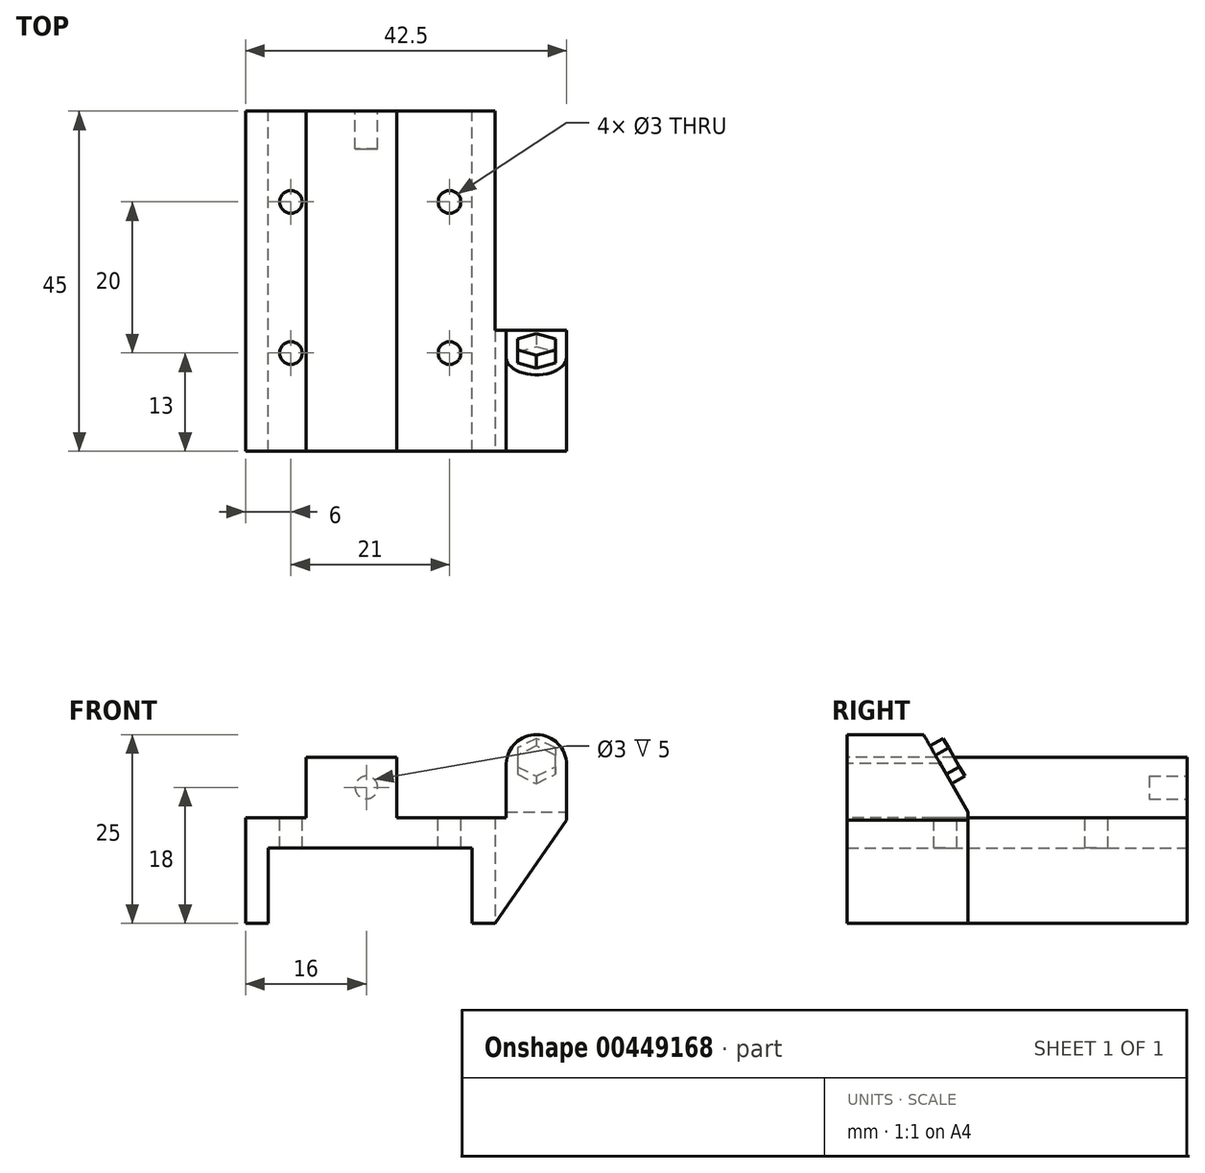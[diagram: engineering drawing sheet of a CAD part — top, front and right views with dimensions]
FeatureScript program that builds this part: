
annotation { "Feature Type Name" : "Feature", "Feature Type Description" : "" }
export const myFeature = defineFeature(function(context is Context, id is Id, definition is map)
    precondition{}
    {
        {
            var Q0;
            Q0=qCreatedBy(makeId("Top.planeOp"),FACE);
            var sketch = newSketch(context, id + "F0", { "sketchPlane" : qUnion([Q0]), "disableImprinting" : false});
            skLineSegment(sketch, "E0.bottom", {"start": v(-16.5, 22.5) * mm, "end": v(16.5, 22.5) * mm});
            skLineSegment(sketch, "E0.top", {"start": v(-16.5, -22.5) * mm, "end": v(16.5, -22.5) * mm});
            skLineSegment(sketch, "E0.left", {"start": v(-16.5, 22.5) * mm, "end": v(-16.5, -22.5) * mm});
            skLineSegment(sketch, "E0.right", {"start": v(16.5, 22.5) * mm, "end": v(16.5, -22.5) * mm});
            skPoint(sketch, "E1", {"position": v(0, 22.5) * mm});
            skPoint(sketch, "E2", {"position": v(16.5, 0) * mm});
            skSolve(sketch);
        }
        {
            var Q0;
            Q0=makeQuery(id+"F0.imprint","IMPRINT",FACE,{"disambiguationData":[TD([[makeQuery(id+"F0.imprint","IMPRINT",EDGE,{"derivedFrom":sQuery(id+"F0.wireOp",EDGE,"E0.bottom")}),-1.0]])]});
            extrude(context, id + "F1", {"entities" : qUnion([Q0]), "depth" : 14 * mm});
        }
        {
            var Q0;
            Q0=makeQuery(id+"F1.opExtrude","CAP_FACE",FACE,{"disambiguationData":[OSD([sQuery(id+"F0.wireOp",EDGE,"E0.bottom"),sQuery(id+"F0.wireOp",EDGE,"E0.top"),sQuery(id+"F0.wireOp",EDGE,"E0.left"),sQuery(id+"F0.wireOp",EDGE,"E0.right")])],"isStart":true});
            var sketch = newSketch(context, id + "F2", { "sketchPlane" : qUnion([Q0]), "disableImprinting" : false});
            skLineSegment(sketch, "E3.bottom", {"start": v(-13.5, 33.53) * mm, "end": v(13.5, 33.53) * mm});
            skLineSegment(sketch, "E3.top", {"start": v(-13.5, -30.84) * mm, "end": v(13.5, -30.84) * mm});
            skLineSegment(sketch, "E3.left", {"start": v(-13.5, 33.53) * mm, "end": v(-13.5, -30.84) * mm});
            skLineSegment(sketch, "E3.right", {"start": v(13.5, 33.53) * mm, "end": v(13.5, -30.84) * mm});
            skPoint(sketch, "E4", {"position": v(0, 33.53) * mm});
            skSolve(sketch);
        }
        {
            var Q0;
            {var subQ0=sQuery(id+"F2.wireOp",EDGE,"E3.bottom");Q0=makeQuery(id+"F2.imprint","IMPRINT",FACE,{"disambiguationData":[TD([[makeQuery(id+"F2.imprint","IMPRINT",EDGE,{"derivedFrom":subQ0}),-1.0]])]});}
            var Q1;
            {var subQ0=sQuery(id+"F2.wireOp",EDGE,"E3.left");var subQ1=makeQuery(id+"F1.opExtrude","CAP_EDGE",EDGE,{"disambiguationData":[OSD([sQuery(id+"F0.wireOp",EDGE,"E0.top")])],"isStart":true});var subQ2=makeQuery(id+"F2.imprint","INTERSECT",VERTEX,{"derivedFrom":[subQ1,subQ0]});Q1=makeQuery(id+"F2.imprint","IMPRINT",FACE,{"disambiguationData":[TD([[makeQuery(id+"F2.imprint","IMPRINT",EDGE,{"disambiguationData":[TD([[subQ2,-1.0]])],"derivedFrom":subQ0}),1.0]])]});}
            var Q2;
            {var subQ0=sQuery(id+"F2.wireOp",EDGE,"E3.top");Q2=makeQuery(id+"F2.imprint","IMPRINT",FACE,{"disambiguationData":[TD([[makeQuery(id+"F2.imprint","IMPRINT",EDGE,{"derivedFrom":subQ0}),1.0]])]});}
            extrude(context, id + "F3", {"entities" : qUnion([Q0, Q1, Q2]), "operationType" : NewBodyOperationType.REMOVE, "oppositeDirection" : true, "depth" : 10 * mm});
        }
        {
            var Q0;
            Q0=makeQuery(id+"F1.opExtrude","CAP_FACE",FACE,{"disambiguationData":[OSD([sQuery(id+"F0.wireOp",EDGE,"E0.bottom"),sQuery(id+"F0.wireOp",EDGE,"E0.top"),sQuery(id+"F0.wireOp",EDGE,"E0.left"),sQuery(id+"F0.wireOp",EDGE,"E0.right")])],"isStart":false});
            var sketch = newSketch(context, id + "F4", { "sketchPlane" : qUnion([Q0])});
            skLineSegment(sketch, "E5.bottom", {"start": v(3.5, 22.5) * mm, "end": v(-8.5, 22.5) * mm});
            skLineSegment(sketch, "E5.top", {"start": v(3.5, -22.5) * mm, "end": v(-8.5, -22.5) * mm});
            skLineSegment(sketch, "E5.left", {"start": v(3.5, 22.5) * mm, "end": v(3.5, -22.5) * mm});
            skLineSegment(sketch, "E5.right", {"start": v(-8.5, 22.5) * mm, "end": v(-8.5, -22.5) * mm});
            skSolve(sketch);
        }
        {
            var Q0;
            Q0=makeQuery(id+"F4.imprint","IMPRINT",FACE,{"disambiguationData":[TD([[makeQuery(id+"F4.imprint","IMPRINT",EDGE,{"derivedFrom":sQuery(id+"F4.wireOp",EDGE,"E5.bottom")}),-1.0]])]});
            extrude(context, id + "F5", {"entities" : qUnion([Q0]), "operationType" : NewBodyOperationType.ADD, "depth" : 8 * mm});
        }
        {
            var Q0;
            {var subQ0=sQuery(id+"F0.wireOp",EDGE,"E0.right");var subQ1=sQuery(id+"F0.wireOp",EDGE,"E0.top");var subQ2=sQuery(id+"F0.wireOp",EDGE,"E0.bottom");Q0=makeQuery(id+"F5.boolean.opBoolean","SPLIT",FACE,{"disambiguationData":[TD([makeQuery(id+"F1.opExtrude","SWEPT_FACE",FACE,{"disambiguationData":[OSD([subQ0])]})])],"derivedFrom":makeQuery(id+"F1.opExtrude","CAP_FACE",FACE,{"disambiguationData":[OSD([subQ2,subQ1,sQuery(id+"F0.wireOp",EDGE,"E0.left"),subQ0])],"isStart":false})});}
            var sketch = newSketch(context, id + "F6", { "sketchPlane" : qUnion([Q0])});
            skCircle(sketch, "E6", {"center": v(10.5, -9.5) * mm, "radius": 1.5 * mm});
            skCircle(sketch, "E7", {"center": v(10.5, 10.5) * mm, "radius": 1.5 * mm});
            skCircle(sketch, "E8", {"center": v(-10.5, 10.5) * mm, "radius": 1.5 * mm});
            skCircle(sketch, "E9", {"center": v(-10.5, -9.5) * mm, "radius": 1.5 * mm});
            skSolve(sketch);
        }
        {
            var Q0;
            Q0=makeQuery(id+"F6.imprint","IMPRINT",FACE,{"disambiguationData":[TD([[makeQuery(id+"F6.imprint","IMPRINT",EDGE,{"derivedFrom":sQuery(id+"F6.wireOp",EDGE,"E7")}),1.0]])]});
            var Q1;
            Q1=makeQuery(id+"F6.imprint","IMPRINT",FACE,{"disambiguationData":[TD([[makeQuery(id+"F6.imprint","IMPRINT",EDGE,{"derivedFrom":sQuery(id+"F6.wireOp",EDGE,"E6")}),1.0]])]});
            var Q2;
            Q2=makeQuery(id+"F6.imprint","IMPRINT",FACE,{"disambiguationData":[TD([[makeQuery(id+"F6.imprint","IMPRINT",EDGE,{"derivedFrom":sQuery(id+"F6.wireOp",EDGE,"E9")}),1.0]])]});
            var Q3;
            Q3=makeQuery(id+"F6.imprint","IMPRINT",FACE,{"disambiguationData":[TD([[makeQuery(id+"F6.imprint","IMPRINT",EDGE,{"derivedFrom":sQuery(id+"F6.wireOp",EDGE,"E8")}),1.0]])]});
            extrude(context, id + "F7", {"entities" : qUnion([Q0, Q1, Q2, Q3]), "operationType" : NewBodyOperationType.REMOVE, "oppositeDirection" : true, "depth" : 25 * mm});
        }
        {
            var Q0;
            Q0=makeQuery(id+"F5.boolean.opBoolean","MERGE",FACE,{"derivedFrom":[makeQuery(id+"F1.opExtrude","SWEPT_FACE",FACE,{"disambiguationData":[OSD([sQuery(id+"F0.wireOp",EDGE,"E0.bottom")])]}),makeQuery(id+"F5.opExtrude","SWEPT_FACE",FACE,{"disambiguationData":[OSD([sQuery(id+"F4.wireOp",EDGE,"E5.bottom")])]})]});
            var sketch = newSketch(context, id + "F8", { "sketchPlane" : qUnion([Q0])});
            skCircle(sketch, "E10", {"center": v(0.5, 18) * mm, "radius": 1.5 * mm});
            skSolve(sketch);
        }
        {
            var Q0;
            Q0=makeQuery(id+"F8.imprint","IMPRINT",FACE,{"disambiguationData":[TD([[makeQuery(id+"F8.imprint","IMPRINT",EDGE,{"derivedFrom":sQuery(id+"F8.wireOp",EDGE,"E10")}),1.0]])]});
            extrude(context, id + "F9", {"entities" : qUnion([Q0]), "operationType" : NewBodyOperationType.REMOVE, "oppositeDirection" : true, "depth" : 5 * mm});
        }
        {
            var Q0;
            Q0=makeQuery(id+"F5.boolean.opBoolean","MERGE",FACE,{"derivedFrom":[makeQuery(id+"F1.opExtrude","SWEPT_FACE",FACE,{"disambiguationData":[OSD([sQuery(id+"F0.wireOp",EDGE,"E0.top")])]}),makeQuery(id+"F5.opExtrude","SWEPT_FACE",FACE,{"disambiguationData":[OSD([sQuery(id+"F4.wireOp",EDGE,"E5.top")])]})]});
            var sketch = newSketch(context, id + "F10", { "sketchPlane" : qUnion([Q0])});
            skSolve(sketch);
        }
        {
            var Q0;
            {var subQ0=sQuery(id+"F4.wireOp",EDGE,"E5.top");Q0=makeQuery(id+"F10.imprint","IMPRINT",FACE,{"disambiguationData":[TD([[makeQuery(id+"F10.imprint","IMPRINT",EDGE,{"derivedFrom":makeQuery(id+"F5.opExtrude","CAP_EDGE",EDGE,{"disambiguationData":[OSD([subQ0])],"isStart":false})}),-1.0]])]});}
            var sketch = newSketch(context, id + "F11", { "sketchPlane" : qUnion([Q0])});
            skLineSegment(sketch, "E11.0", {"start": v(3.5, 14) * mm, "end": v(16.5, 14) * mm});
            skPoint(sketch, "E12.0", {"position": v(-12.5, 14) * mm});
            skLineSegment(sketch, "E13.0", {"start": v(-16.5, 14) * mm, "end": v(-8.5, 14) * mm});
            skLineSegment(sketch, "E14", {"start": v(26, 14) * mm, "end": v(26, 13.68) * mm});
            skLineSegment(sketch, "E15.0", {"start": v(13.5, 0) * mm, "end": v(13.5, 10) * mm});
            skPoint(sketch, "E16.0", {"position": v(16.5, 0) * mm});
            skLineSegment(sketch, "E17", {"start": v(16.5, 0) * mm, "end": v(26, 13.68) * mm});
            skLineSegment(sketch, "E18", {"start": v(16.5, 14) * mm, "end": v(26, 14) * mm});
            skPoint(sketch, "E19.orphan", {"position": v(26, 14.32) * mm});
            skSolve(sketch);
        }
        {
            var Q0;
            Q0=makeQuery(id+"F11.imprint","IMPRINT",FACE,{"disambiguationData":[TD([[makeQuery(id+"F11.imprint","IMPRINT",EDGE,{"derivedFrom":sQuery(id+"F11.wireOp",EDGE,"E14")}),-1.0]])]});
            extrude(context, id + "F12", {"entities" : qUnion([Q0]), "operationType" : NewBodyOperationType.ADD, "oppositeDirection" : true, "depth" : 16 * mm});
        }
        {
            var Q0;
            {var subQ0=sQuery(id+"F0.wireOp",EDGE,"E0.top");Q0=makeQuery(id+"F12.boolean.opBoolean","MERGE",FACE,{"derivedFrom":[makeQuery(id+"F5.boolean.opBoolean","MERGE",FACE,{"derivedFrom":[makeQuery(id+"F1.opExtrude","SWEPT_FACE",FACE,{"disambiguationData":[OSD([subQ0])]}),makeQuery(id+"F5.opExtrude","SWEPT_FACE",FACE,{"disambiguationData":[OSD([sQuery(id+"F4.wireOp",EDGE,"E5.top")])]})]}),makeQuery(id+"F12.opExtrude","CAP_FACE",FACE,{"disambiguationData":[OSD([subQ0,sQuery(id+"F0.wireOp",EDGE,"E0.right"),sQuery(id+"F11.wireOp",EDGE,"E14"),sQuery(id+"F11.wireOp",EDGE,"E17"),sQuery(id+"F11.wireOp",EDGE,"E18")])],"isStart":true})]});}
            var sketch = newSketch(context, id + "F13", { "sketchPlane" : qUnion([Q0])});
            skArc(sketch, "E20", {"start": v(26, 21) * mm, "mid": v(21.93, 25) * mm, "end": v(18, 20.85) * mm});
            skLineSegment(sketch, "E21", {"start": v(26, 14) * mm, "end": v(26, 21) * mm});
            skLineSegment(sketch, "E22", {"start": v(18, 21.15) * mm, "end": v(18, 14) * mm});
            skLineSegment(sketch, "E23", {"start": v(18, 14) * mm, "end": v(26, 14) * mm});
            skSolve(sketch);
        }
        {
            var Q0;
            {var subQ7=sQuery(id+"F13.wireOp",EDGE,"E21");Q0=makeQuery(id+"F13.imprint","IMPRINT",FACE,{"disambiguationData":[TD([[makeQuery(id+"F13.imprint","IMPRINT",EDGE,{"derivedFrom":subQ7}),1.0]])]});}
            extrude(context, id + "F14", {"entities" : qUnion([Q0]), "operationType" : NewBodyOperationType.ADD, "oppositeDirection" : true, "depth" : 16 * mm});
        }
        {
            var Q0;
            Q0=makeQuery(id+"F14.boolean.opBoolean","MERGE",FACE,{"derivedFrom":[makeQuery(id+"F12.opExtrude","SWEPT_FACE",FACE,{"disambiguationData":[OSD([sQuery(id+"F11.wireOp",EDGE,"E14")])]}),makeQuery(id+"F14.opExtrude","SWEPT_FACE",FACE,{"disambiguationData":[OSD([sQuery(id+"F13.wireOp",EDGE,"E21")])]})]});
            var sketch = newSketch(context, id + "F15", { "sketchPlane" : qUnion([Q0])});
            skLineSegment(sketch, "E24", {"start": v(-15.02, 29.54) * mm, "end": v(-4.6, 11.5) * mm});
            skLineSegment(sketch, "E25", {"start": v(-4.6, 11.5) * mm, "end": v(5.55, 17.37) * mm});
            skLineSegment(sketch, "E26", {"start": v(5.55, 17.37) * mm, "end": v(-5.35, 36.26) * mm});
            skLineSegment(sketch, "E27", {"start": v(-5.35, 36.26) * mm, "end": v(-15.02, 29.54) * mm});
            skSolve(sketch);
        }
        {
            var Q0;
            {var subQ0=sQuery(id+"F15.wireOp",EDGE,"E25");Q0=makeQuery(id+"F15.imprint","IMPRINT",FACE,{"disambiguationData":[TD([[makeQuery(id+"F15.imprint","IMPRINT",EDGE,{"derivedFrom":subQ0}),1.0]])]});}
            var Q1;
            {var subQ0=sQuery(id+"F15.wireOp",EDGE,"E24");var subQ1=sQuery(id+"F13.wireOp",EDGE,"E21");var subQ2=makeQuery(id+"F14.opExtrude","SWEPT_EDGE",EDGE,{"disambiguationData":[OSD([sQuery(id+"F13.wireOp",EDGE,"E20"),subQ1])]});var subQ3=makeQuery(id+"F15.imprint","INTERSECT",VERTEX,{"derivedFrom":[subQ2,subQ0]});Q1=makeQuery(id+"F15.imprint","IMPRINT",FACE,{"disambiguationData":[TD([[makeQuery(id+"F15.imprint","IMPRINT",EDGE,{"disambiguationData":[TD([[subQ3,-1.0]])],"derivedFrom":subQ0}),1.0]])]});}
            extrude(context, id + "F16", {"entities" : qUnion([Q0, Q1]), "operationType" : NewBodyOperationType.REMOVE, "oppositeDirection" : true, "depth" : 8 * mm});
        }
        {
            var Q0;
            Q0=makeQuery(id+"F16.boolean.opBoolean","COPY",FACE,{"derivedFrom":makeQuery(id+"F16.opExtrude","SWEPT_FACE",FACE,{"disambiguationData":[OSD([sQuery(id+"F15.wireOp",EDGE,"E24")])]})});
            var sketch = newSketch(context, id + "F17", { "sketchPlane" : qUnion([Q0])});
            skCircle(sketch, "E28.cCircle", {"center": v(-22, 23.23) * mm, "radius": 2.5 * mm, "construction": true});
            skLineSegment(sketch, "E28.0", {"start": v(-19.5, 24.67) * mm, "end": v(-19.5, 21.79) * mm});
            skLineSegment(sketch, "E28.1", {"start": v(-19.5, 21.79) * mm, "end": v(-22, 20.34) * mm});
            skLineSegment(sketch, "E28.2", {"start": v(-22, 20.34) * mm, "end": v(-24.5, 21.79) * mm});
            skLineSegment(sketch, "E28.3", {"start": v(-24.5, 21.79) * mm, "end": v(-24.5, 24.67) * mm});
            skLineSegment(sketch, "E28.4", {"start": v(-24.5, 24.67) * mm, "end": v(-22, 26.12) * mm});
            skLineSegment(sketch, "E28.5", {"start": v(-22, 26.12) * mm, "end": v(-19.5, 24.67) * mm});
            skPoint(sketch, "E28.0.midPoint", {"position": v(-19.5, 23.23) * mm});
            skSolve(sketch);
        }
        {
            var Q0;
            Q0=makeQuery(id+"F17.imprint","IMPRINT",FACE,{"disambiguationData":[TD([[makeQuery(id+"F17.imprint","IMPRINT",EDGE,{"derivedFrom":sQuery(id+"F17.wireOp",EDGE,"E28.0")}),-1.0]])]});
            extrude(context, id + "F18", {"entities" : qUnion([Q0]), "operationType" : NewBodyOperationType.ADD, "depth" : 2 * mm});
        }
        {
            var Q0;
            Q0=makeQuery(id+"F18.opExtrude","SWEPT_FACE",FACE,{"disambiguationData":[OSD([sQuery(id+"F17.wireOp",EDGE,"E28.3")])]});
            cPlane(context, id + "F19", {"entities" : qUnion([Q0]), "cplaneType" : CPlaneType.OFFSET, "offset" : 2.5 * mm, "oppositeDirection" : true, "width" : 150 * mm, "height" : 150 * mm});
        }
    });
